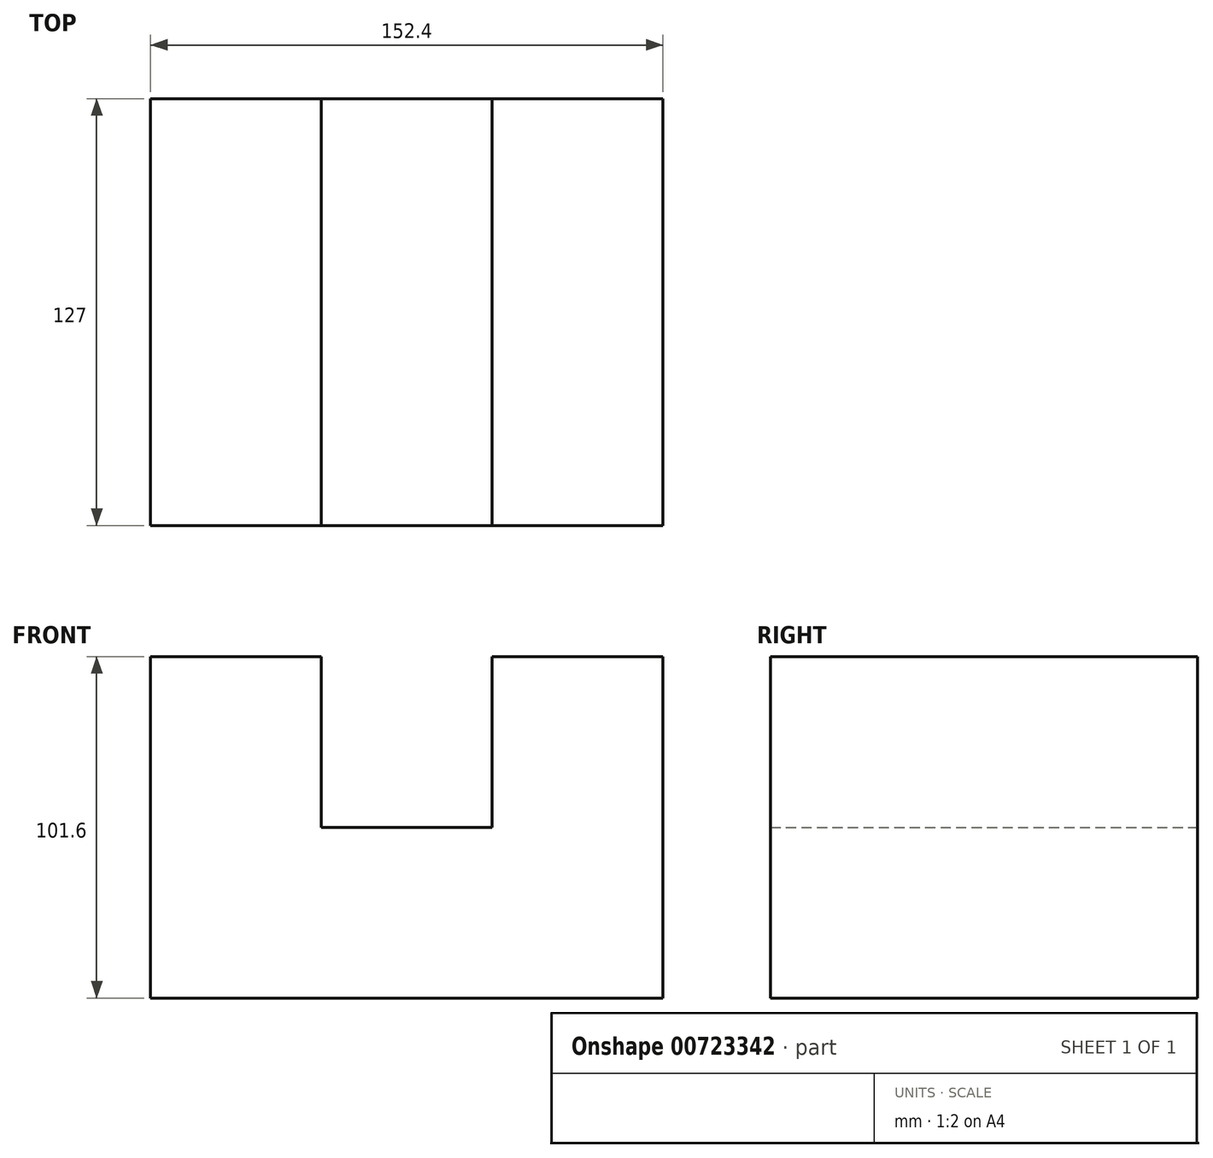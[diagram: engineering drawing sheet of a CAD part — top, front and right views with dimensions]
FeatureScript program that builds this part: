
annotation { "Feature Type Name" : "Feature", "Feature Type Description" : "" }
export const myFeature = defineFeature(function(context is Context, id is Id, definition is map)
    precondition{}
    {
        {
            var Q0;
            Q0=qCreatedBy(makeId("Front.planeOp"),FACE);
            var sketch = newSketch(context, id + "F0", { "sketchPlane" : qUnion([Q0])});
            skLineSegment(sketch, "E0", {"start": v(-93.92, -101.6) * mm, "end": v(58.48, -101.6) * mm});
            skLineSegment(sketch, "E1", {"start": v(-93.92, -101.6) * mm, "end": v(-93.92, 0) * mm});
            skLineSegment(sketch, "E2", {"start": v(-93.92, 0) * mm, "end": v(-43.12, 0) * mm});
            skLineSegment(sketch, "E3", {"start": v(-43.12, 0) * mm, "end": v(-43.12, -50.8) * mm});
            skLineSegment(sketch, "E4", {"start": v(-43.12, -50.8) * mm, "end": v(7.68, -50.8) * mm});
            skLineSegment(sketch, "E5", {"start": v(7.68, -50.8) * mm, "end": v(7.68, 0) * mm});
            skLineSegment(sketch, "E6", {"start": v(7.68, 0) * mm, "end": v(58.48, 0) * mm});
            skLineSegment(sketch, "E7", {"start": v(58.48, 0) * mm, "end": v(58.48, -101.6) * mm});
            skSolve(sketch);
        }
        {
            var Q0;
            Q0=makeQuery(id+"F0.imprint","IMPRINT",FACE,{"disambiguationData":[TD([[makeQuery(id+"F0.imprint","IMPRINT",EDGE,{"derivedFrom":sQuery(id+"F0.wireOp",EDGE,"E0")}),1.0]])]});
            extrude(context, id + "F1", {"entities" : qUnion([Q0]), "depth" : 127 * mm, "offsetDistance" : 25.4 * mm});
        }
    });
